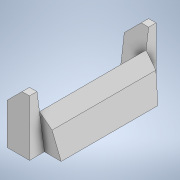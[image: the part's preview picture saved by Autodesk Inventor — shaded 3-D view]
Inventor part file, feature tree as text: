
AUTODESK INVENTOR PART (.ipt)
format: ipt  version: 2021 (Build 250183000, 183)  size: 165,376 bytes
history: native  units: in
note: dims shown in document units (in); Inventor stores cm internally (conversion verified against a paired STEP export)
features: extrude x7, sketch x7
ambient origin geometry x8: Origin, YZ Plane, XZ Plane, XY Plane, X Axis, Y Axis, Z Axis, Center Point
bodies: Solid1 (feature_tree)
feature tree (14):
  extrude  "Extrusion1"  Depth=1.0236in TaperAngle=0.0deg
  extrude  "Extrusion2"  Depth=0.5906in
  extrude  "Extrusion3"  Depth=0.2362in
  extrude  "Extrusion4"  Depth=0.345in TaperAngle=0.0deg
  extrude  "Extrusion5"  Depth=0.4331in
  extrude  "Extrusion6"  Depth=0.4075in TaperAngle=0.0deg
  extrude  "Extrusion7"  [1 undecoded]
  sketch  "Sketch1"  dims[d2=45.0deg d3=1.0236in d4=0.0in]
  sketch  "Sketch2"  dims[d6=0.5906in d7=0.0787in]
  sketch  "Sketch3"  dims[d8=0.2362in d9=0.4331in]
  sketch  "Sketch4"  dims[d10=0.1575in d11=0.0in d12=0.345in d13=0.0in]
  sketch  "Sketch5"  dims[d14=0.345in d15=0.0in d18=0.4331in]
  sketch  "Sketch6"  dims[d19=0.1575in d20=0.0in d21=0.4075in d22=0.0in]
  sketch  "Sketch7"  dims[d23=0.4075in d24=0.0in]
note: 1 required parameter value undecoded (feature->parameter linkage not recoverable at this tier; creation-order binding heuristic only, values carry confidence <= 0.55)
